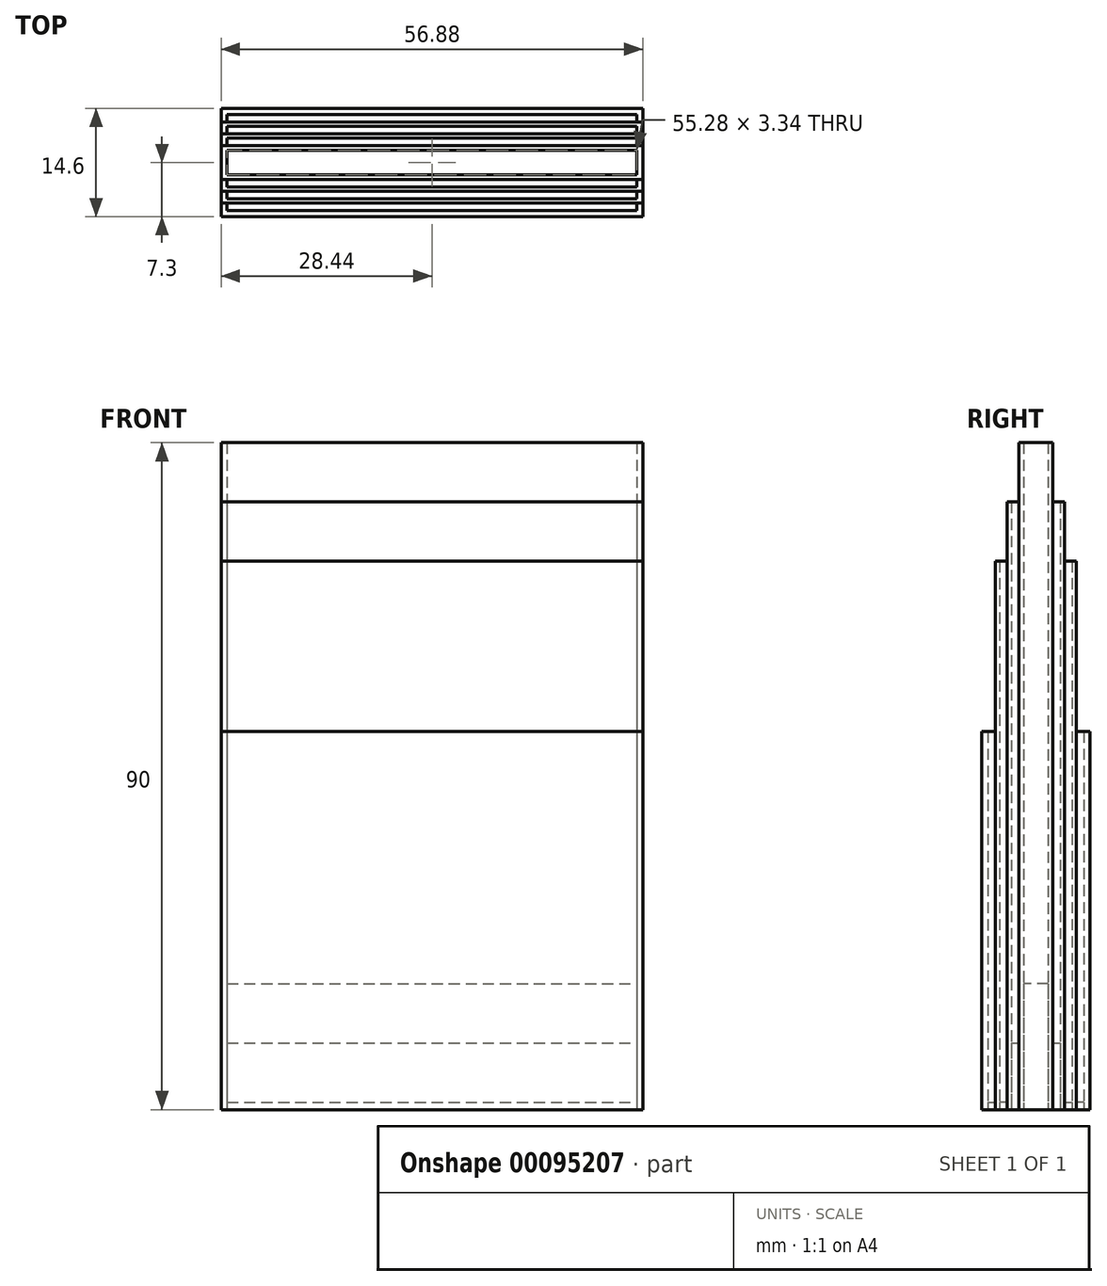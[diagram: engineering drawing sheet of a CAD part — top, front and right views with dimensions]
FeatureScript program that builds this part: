
annotation { "Feature Type Name" : "Feature", "Feature Type Description" : "" }
export const myFeature = defineFeature(function(context is Context, id is Id, definition is map)
    precondition{}
    {
        {
            var Q0;
            Q0=qCreatedBy(makeId("Top.planeOp"),FACE);
            var sketch = newSketch(context, id + "F0", { "sketchPlane" : qUnion([Q0])});
            skLineSegment(sketch, "E0.bottom", {"start": v(0, 0) * mm, "end": v(55.28, 0) * mm});
            skLineSegment(sketch, "E0.top", {"start": v(0, 1.01) * mm, "end": v(55.28, 1.01) * mm});
            skLineSegment(sketch, "E0.left", {"start": v(0, 0) * mm, "end": v(0, 1.01) * mm});
            skLineSegment(sketch, "E0.right", {"start": v(55.28, 0) * mm, "end": v(55.28, 1.01) * mm});
            skLineSegment(sketch, "E1", {"start": v(0, 1.01) * mm, "end": v(0, 1.61) * mm});
            skLineSegment(sketch, "E2", {"start": v(0, 1.61) * mm, "end": v(55.28, 1.61) * mm});
            skLineSegment(sketch, "E3", {"start": v(55.28, 1.61) * mm, "end": v(55.28, 1.01) * mm});
            skLineSegment(sketch, "E4", {"start": v(0, 1.61) * mm, "end": v(0, 2.62) * mm});
            skLineSegment(sketch, "E5", {"start": v(0, 2.62) * mm, "end": v(55.28, 2.62) * mm});
            skLineSegment(sketch, "E6", {"start": v(55.28, 2.62) * mm, "end": v(55.28, 1.61) * mm});
            skLineSegment(sketch, "E7", {"start": v(0, 0) * mm, "end": v(0, -0.6) * mm});
            skLineSegment(sketch, "E8", {"start": v(0, -0.6) * mm, "end": v(55.28, -0.6) * mm});
            skLineSegment(sketch, "E9", {"start": v(55.28, -0.6) * mm, "end": v(55.28, 0) * mm});
            skLineSegment(sketch, "E10", {"start": v(0, -0.6) * mm, "end": v(0, -3.94) * mm});
            skLineSegment(sketch, "E11", {"start": v(0, -3.94) * mm, "end": v(55.28, -3.94) * mm});
            skLineSegment(sketch, "E12", {"start": v(55.28, -3.94) * mm, "end": v(55.28, -0.6) * mm});
            skLineSegment(sketch, "E13", {"start": v(0, -3.94) * mm, "end": v(0, -4.54) * mm});
            skLineSegment(sketch, "E14", {"start": v(0, -4.54) * mm, "end": v(0, -5.55) * mm});
            skLineSegment(sketch, "E15", {"start": v(0, -5.55) * mm, "end": v(0, -6.15) * mm});
            skLineSegment(sketch, "E16", {"start": v(0, -6.15) * mm, "end": v(0, -7.16) * mm});
            skLineSegment(sketch, "E17", {"start": v(0, -7.16) * mm, "end": v(55.28, -7.16) * mm});
            skLineSegment(sketch, "E18", {"start": v(55.28, -7.16) * mm, "end": v(55.28, -3.94) * mm});
            skLineSegment(sketch, "E19", {"start": v(0, -4.54) * mm, "end": v(55.28, -4.54) * mm});
            skLineSegment(sketch, "E20", {"start": v(0, -5.55) * mm, "end": v(55.28, -5.55) * mm});
            skLineSegment(sketch, "E21", {"start": v(0, -6.15) * mm, "end": v(55.28, -6.15) * mm});
            skLineSegment(sketch, "E22", {"start": v(0, -7.16) * mm, "end": v(0, -7.76) * mm});
            skLineSegment(sketch, "E23", {"start": v(0, -7.76) * mm, "end": v(0, -8.77) * mm});
            skLineSegment(sketch, "E24", {"start": v(0, -8.77) * mm, "end": v(55.28, -8.77) * mm});
            skLineSegment(sketch, "E25", {"start": v(55.28, -8.77) * mm, "end": v(55.28, -7.16) * mm});
            skLineSegment(sketch, "E26", {"start": v(0, -7.76) * mm, "end": v(55.28, -7.76) * mm});
            skLineSegment(sketch, "E27", {"start": v(0, 2.62) * mm, "end": v(0, 3.22) * mm});
            skLineSegment(sketch, "E28", {"start": v(0, 3.22) * mm, "end": v(0, 4.23) * mm});
            skLineSegment(sketch, "E29", {"start": v(0, 4.23) * mm, "end": v(55.28, 4.23) * mm});
            skLineSegment(sketch, "E30", {"start": v(55.28, 4.23) * mm, "end": v(55.28, 2.62) * mm});
            skLineSegment(sketch, "E31", {"start": v(0, 3.22) * mm, "end": v(55.28, 3.22) * mm});
            skLineSegment(sketch, "E32.0", {"start": v(-0.8, -7.76) * mm, "end": v(-0.8, -9.57) * mm});
            skLineSegment(sketch, "E32.1", {"start": v(-0.8, -9.57) * mm, "end": v(56.08, -9.57) * mm});
            skLineSegment(sketch, "E32.2", {"start": v(56.08, -9.57) * mm, "end": v(56.08, -7.01) * mm});
            skLineSegment(sketch, "E32.3", {"start": v(56.08, -7.01) * mm, "end": v(56.08, -3.86) * mm});
            skLineSegment(sketch, "E32.6", {"start": v(56.08, 5.03) * mm, "end": v(56.08, 2.48) * mm});
            skLineSegment(sketch, "E32.10", {"start": v(-0.8, 5.03) * mm, "end": v(56.08, 5.03) * mm});
            skLineSegment(sketch, "E32.11", {"start": v(-0.8, -7.36) * mm, "end": v(-0.8, -7.76) * mm});
            skLineSegment(sketch, "E32.12", {"start": v(-0.8, -6.15) * mm, "end": v(-0.8, -7.36) * mm});
            skLineSegment(sketch, "E32.13", {"start": v(-0.8, -5.7) * mm, "end": v(-0.8, -6.15) * mm});
            skLineSegment(sketch, "E32.14", {"start": v(-0.8, -4.54) * mm, "end": v(-0.8, -5.7) * mm});
            skLineSegment(sketch, "E32.15", {"start": v(-0.8, -4.04) * mm, "end": v(-0.8, -4.54) * mm});
            skLineSegment(sketch, "E32.16", {"start": v(-0.8, -0.6) * mm, "end": v(-0.8, -4.04) * mm});
            skLineSegment(sketch, "E32.17", {"start": v(-0.8, 0) * mm, "end": v(-0.8, -0.6) * mm});
            skLineSegment(sketch, "E32.18", {"start": v(-0.8, 0) * mm, "end": v(-0.8, 1.06) * mm});
            skLineSegment(sketch, "E32.19", {"start": v(-0.8, 1.06) * mm, "end": v(-0.8, 1.61) * mm});
            skLineSegment(sketch, "E32.20", {"start": v(-0.8, 1.61) * mm, "end": v(-0.8, 2.72) * mm});
            skLineSegment(sketch, "E32.21", {"start": v(-0.8, 2.72) * mm, "end": v(-0.8, 3.22) * mm});
            skLineSegment(sketch, "E32.22", {"start": v(-0.8, 3.22) * mm, "end": v(-0.8, 5.03) * mm});
            skLineSegment(sketch, "E33", {"start": v(55.28, 3.22) * mm, "end": v(56.08, 3.22) * mm});
            skLineSegment(sketch, "E34", {"start": v(55.28, -7.76) * mm, "end": v(56.08, -7.76) * mm});
            skLineSegment(sketch, "E35", {"start": v(55.28, -6.15) * mm, "end": v(56.08, -6.15) * mm});
            skLineSegment(sketch, "E36", {"start": v(55.28, -4.54) * mm, "end": v(56.08, -4.54) * mm});
            skLineSegment(sketch, "E37", {"start": v(0, -7.76) * mm, "end": v(-0.8, -7.76) * mm});
            skLineSegment(sketch, "E38", {"start": v(0, -6.15) * mm, "end": v(-0.8, -6.15) * mm});
            skLineSegment(sketch, "E39", {"start": v(0, -4.54) * mm, "end": v(-0.8, -4.54) * mm});
            skLineSegment(sketch, "E40", {"start": v(0, 0) * mm, "end": v(-0.8, 0) * mm});
            skLineSegment(sketch, "E41", {"start": v(0, 1.61) * mm, "end": v(-0.8, 1.61) * mm});
            skLineSegment(sketch, "E42", {"start": v(0, 3.22) * mm, "end": v(-0.8, 3.22) * mm});
            skLineSegment(sketch, "E43", {"start": v(56.08, 2.48) * mm, "end": v(56.08, -3.86) * mm});
            skLineSegment(sketch, "E44", {"start": v(55.28, 0) * mm, "end": v(56.08, 0) * mm});
            skLineSegment(sketch, "E45", {"start": v(55.28, 1.61) * mm, "end": v(56.08, 1.61) * mm});
            skSolve(sketch);
        }
        {
            var Q0;
            Q0=makeQuery(id+"F0.imprint","IMPRINT",FACE,{"disambiguationData":[TD([[makeQuery(id+"F0.imprint","IMPRINT",EDGE,{"derivedFrom":sQuery(id+"F0.wireOp",EDGE,"E28")}),-1.0]])]});
            var Q1;
            Q1=makeQuery(id+"F0.imprint","IMPRINT",FACE,{"disambiguationData":[TD([[makeQuery(id+"F0.imprint","IMPRINT",EDGE,{"derivedFrom":sQuery(id+"F0.wireOp",EDGE,"E2")}),1.0]])]});
            var Q2;
            Q2=makeQuery(id+"F0.imprint","IMPRINT",FACE,{"disambiguationData":[TD([[makeQuery(id+"F0.imprint","IMPRINT",EDGE,{"derivedFrom":sQuery(id+"F0.wireOp",EDGE,"E16")}),1.0]])]});
            var Q3;
            Q3=makeQuery(id+"F0.imprint","IMPRINT",FACE,{"disambiguationData":[TD([[makeQuery(id+"F0.imprint","IMPRINT",EDGE,{"derivedFrom":sQuery(id+"F0.wireOp",EDGE,"E23")}),1.0]])]});
            extrude(context, id + "F1", {"entities" : qUnion([Q0, Q1, Q2, Q3]), "depth" : 1 * mm});
        }
        {
            var Q0;
            Q0=makeQuery(id+"F0.imprint","IMPRINT",FACE,{"disambiguationData":[TD([[makeQuery(id+"F0.imprint","IMPRINT",EDGE,{"derivedFrom":sQuery(id+"F0.wireOp",EDGE,"E0.bottom")}),1.0]])]});
            var Q1;
            Q1=makeQuery(id+"F0.imprint","IMPRINT",FACE,{"disambiguationData":[TD([[makeQuery(id+"F0.imprint","IMPRINT",EDGE,{"derivedFrom":sQuery(id+"F0.wireOp",EDGE,"E14")}),1.0]])]});
            extrude(context, id + "F2", {"entities" : qUnion([Q0, Q1]), "depth" : 9 * mm});
        }
        {
            var Q0;
            Q0=makeQuery(id+"F0.imprint","IMPRINT",FACE,{"disambiguationData":[TD([[makeQuery(id+"F0.imprint","IMPRINT",EDGE,{"derivedFrom":sQuery(id+"F0.wireOp",EDGE,"E8")}),-1.0]])]});
            extrude(context, id + "F3", {"entities" : qUnion([Q0]), "depth" : 17 * mm});
        }
        {
            var Q0;
            Q0=makeQuery(id+"F0.imprint","IMPRINT",FACE,{"disambiguationData":[TD([[makeQuery(id+"F0.imprint","IMPRINT",EDGE,{"derivedFrom":sQuery(id+"F0.wireOp",EDGE,"E28")}),1.0]])]});
            var Q1;
            Q1=makeQuery(id+"F0.imprint","IMPRINT",FACE,{"disambiguationData":[TD([[makeQuery(id+"F0.imprint","IMPRINT",EDGE,{"derivedFrom":sQuery(id+"F0.wireOp",EDGE,"E23")}),-1.0]])]});
            extrude(context, id + "F4", {"entities" : qUnion([Q0, Q1]), "depth" : 51 * mm});
        }
        {
            var Q0;
            Q0=makeQuery(id+"F0.imprint","IMPRINT",FACE,{"disambiguationData":[TD([[makeQuery(id+"F0.imprint","IMPRINT",EDGE,{"derivedFrom":sQuery(id+"F0.wireOp",EDGE,"E4")}),1.0]])]});
            var Q1;
            {var subQ0=sQuery(id+"F0.wireOp",EDGE,"E5");Q1=makeQuery(id+"F0.imprint","IMPRINT",FACE,{"disambiguationData":[TD([[makeQuery(id+"F0.imprint","IMPRINT",EDGE,{"derivedFrom":subQ0}),1.0]])]});}
            var Q2;
            {var subQ5=sQuery(id+"F0.wireOp",EDGE,"E6");Q2=makeQuery(id+"F0.imprint","IMPRINT",FACE,{"disambiguationData":[TD([[makeQuery(id+"F0.imprint","IMPRINT",EDGE,{"derivedFrom":subQ5}),1.0]])]});}
            var Q3;
            {var subQ4=sQuery(id+"F0.wireOp",EDGE,"E34");Q3=makeQuery(id+"F0.imprint","IMPRINT",FACE,{"disambiguationData":[TD([[makeQuery(id+"F0.imprint","IMPRINT",EDGE,{"derivedFrom":subQ4}),1.0]])]});}
            var Q4;
            {var subQ0=sQuery(id+"F0.wireOp",EDGE,"E17");Q4=makeQuery(id+"F0.imprint","IMPRINT",FACE,{"disambiguationData":[TD([[makeQuery(id+"F0.imprint","IMPRINT",EDGE,{"derivedFrom":subQ0}),-1.0]])]});}
            var Q5;
            Q5=makeQuery(id+"F0.imprint","IMPRINT",FACE,{"disambiguationData":[TD([[makeQuery(id+"F0.imprint","IMPRINT",EDGE,{"derivedFrom":sQuery(id+"F0.wireOp",EDGE,"E16")}),-1.0]])]});
            extrude(context, id + "F5", {"entities" : qUnion([Q0, Q1, Q2, Q3, Q4, Q5]), "depth" : 74 * mm});
        }
        {
            var Q0;
            Q0=makeQuery(id+"F0.imprint","IMPRINT",FACE,{"disambiguationData":[TD([[makeQuery(id+"F0.imprint","IMPRINT",EDGE,{"derivedFrom":sQuery(id+"F0.wireOp",EDGE,"E0.left")}),1.0]])]});
            var Q1;
            Q1=makeQuery(id+"F0.imprint","IMPRINT",FACE,{"disambiguationData":[TD([[makeQuery(id+"F0.imprint","IMPRINT",EDGE,{"derivedFrom":sQuery(id+"F0.wireOp",EDGE,"E0.top")}),1.0]])]});
            var Q2;
            Q2=makeQuery(id+"F0.imprint","IMPRINT",FACE,{"disambiguationData":[TD([[makeQuery(id+"F0.imprint","IMPRINT",EDGE,{"derivedFrom":sQuery(id+"F0.wireOp",EDGE,"E0.right")}),-1.0]])]});
            var Q3;
            {var subQ0=sQuery(id+"F0.wireOp",EDGE,"E35");Q3=makeQuery(id+"F0.imprint","IMPRINT",FACE,{"disambiguationData":[TD([[makeQuery(id+"F0.imprint","IMPRINT",EDGE,{"derivedFrom":subQ0}),1.0]])]});}
            var Q4;
            Q4=makeQuery(id+"F0.imprint","IMPRINT",FACE,{"disambiguationData":[TD([[makeQuery(id+"F0.imprint","IMPRINT",EDGE,{"derivedFrom":sQuery(id+"F0.wireOp",EDGE,"E15")}),1.0]])]});
            var Q5;
            Q5=makeQuery(id+"F0.imprint","IMPRINT",FACE,{"disambiguationData":[TD([[makeQuery(id+"F0.imprint","IMPRINT",EDGE,{"derivedFrom":sQuery(id+"F0.wireOp",EDGE,"E14")}),-1.0]])]});
            extrude(context, id + "F6", {"entities" : qUnion([Q0, Q1, Q2, Q3, Q4, Q5]), "depth" : 82 * mm});
        }
        {
            var Q0;
            Q0=makeQuery(id+"F0.imprint","IMPRINT",FACE,{"disambiguationData":[TD([[makeQuery(id+"F0.imprint","IMPRINT",EDGE,{"derivedFrom":sQuery(id+"F0.wireOp",EDGE,"E7")}),-1.0]])]});
            var Q1;
            Q1=makeQuery(id+"F0.imprint","IMPRINT",FACE,{"disambiguationData":[TD([[makeQuery(id+"F0.imprint","IMPRINT",EDGE,{"derivedFrom":sQuery(id+"F0.wireOp",EDGE,"E0.bottom")}),-1.0]])]});
            var Q2;
            Q2=makeQuery(id+"F0.imprint","IMPRINT",FACE,{"disambiguationData":[TD([[makeQuery(id+"F0.imprint","IMPRINT",EDGE,{"derivedFrom":sQuery(id+"F0.wireOp",EDGE,"E9")}),-1.0]])]});
            var Q3;
            {var subQ0=sQuery(id+"F0.wireOp",EDGE,"E11");Q3=makeQuery(id+"F0.imprint","IMPRINT",FACE,{"disambiguationData":[TD([[makeQuery(id+"F0.imprint","IMPRINT",EDGE,{"derivedFrom":subQ0}),-1.0]])]});}
            extrude(context, id + "F7", {"entities" : qUnion([Q0, Q1, Q2, Q3]), "depth" : 90 * mm});
        }
    });
